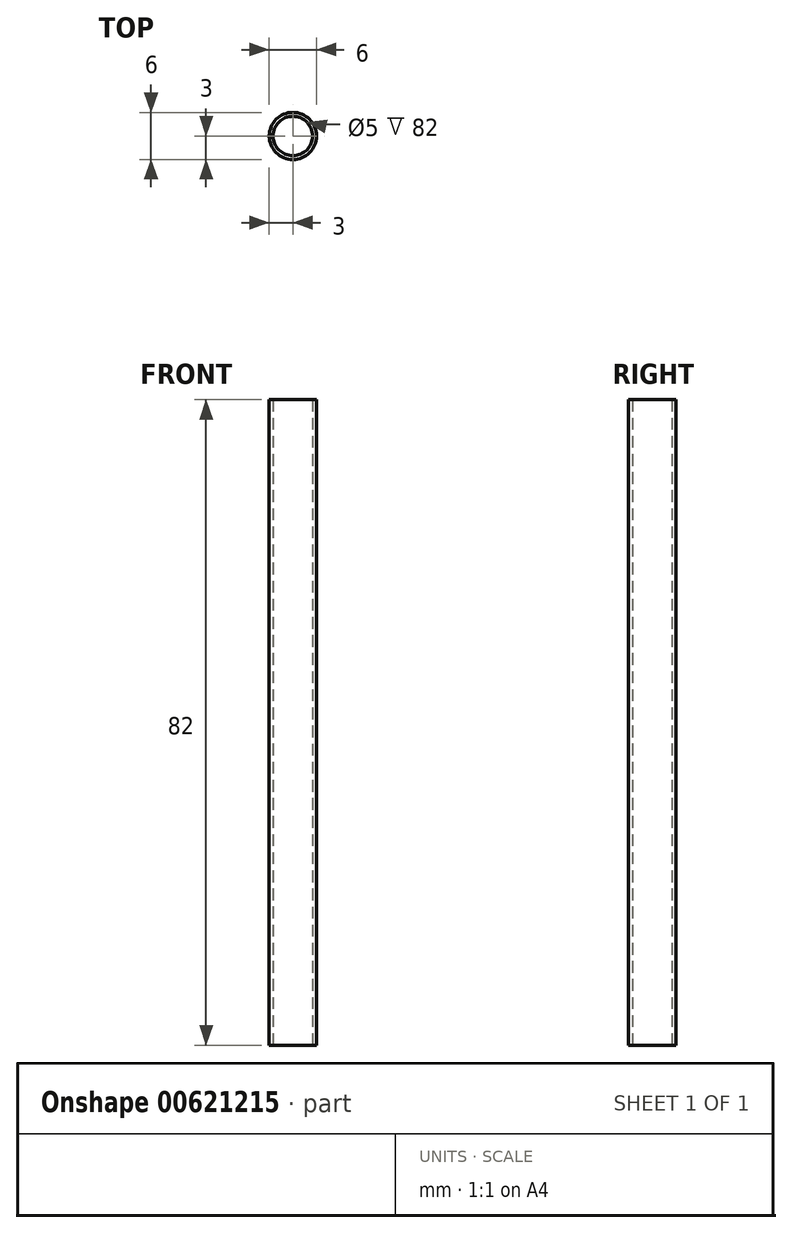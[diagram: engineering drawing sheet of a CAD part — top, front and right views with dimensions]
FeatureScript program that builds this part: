
annotation { "Feature Type Name" : "Feature", "Feature Type Description" : "" }
export const myFeature = defineFeature(function(context is Context, id is Id, definition is map)
    precondition{}
    {
        {
            var Q0;
            Q0=qCreatedBy(makeId("Top.planeOp"),FACE);
            var sketch = newSketch(context, id + "F0", { "sketchPlane" : qUnion([Q0])});
            skCircle(sketch, "E0", {"center": v(0, 0) * mm, "radius": 2.5 * mm});
            skCircle(sketch, "E1", {"center": v(0, 0) * mm, "radius": 3 * mm});
            skSolve(sketch);
        }
        {
            var Q0;
            Q0=makeQuery(id+"F0.imprint","IMPRINT",FACE,{"disambiguationData":[TD([[makeQuery(id+"F0.imprint","IMPRINT",EDGE,{"derivedFrom":sQuery(id+"F0.wireOp",EDGE,"E0")}),-1.0]])]});
            extrude(context, id + "F1", {"entities" : qUnion([Q0]), "depth" : 82 * mm, "offsetDistance" : 25 * mm});
        }
    });
